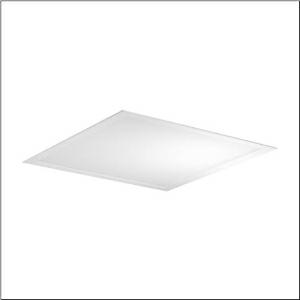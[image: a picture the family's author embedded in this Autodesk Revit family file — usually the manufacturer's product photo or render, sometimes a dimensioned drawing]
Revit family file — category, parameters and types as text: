
# Revit family: apollon_31_square_51mp11w72342
name_source: partatom
category: Lighting Fixtures
units: mm (PartAtom-declared; Revit-internal decimal feet)

## family parameters
Cut with Voids When Loaded = No
Host = Face
Light Source = No
Part Type = Normal
Room Calculation Point = No
Round Connector Dimension = Use Diameter
Shared = No

## types (1)
- Apollon 31 square (1 x LED, 3800 lm, 27.5 W, 3000K)
    Apparent Load = 28 VA
    CIE Flux Codes = 61 87 97 100 100
    Color Rendering = 80
    Color Temperature = 3000K
    Default Elevation = 1800 mm
    Description = Apollon 31 square, office luminaire, primary optical cover: micro prismatic cover, of PMMA, CAT 2 (L<= 3000cd/m²), light emission: direct distribution, primary light characteristic: symmetric, installation type: lay-in mounting, recessed, LED, rated luminous flux: 3.800lm, luminous efficacy: 138lm/W, light colour: 830, colour temperature: 3000K, control gear: ON/OFF, with terminal, 3-pole, mains connection: 220..240V, AC, 50/60Hz, rated input power: 28W, suitable for self-contained emergency lighting element 58DB00B013A with integrated self-test function according to EN 60598-2-22, housing, of aluminium, coated, traffic white (RAL 9016), module: M625, length: 620mm, width: 620mm, height: 62mm, housing upper side, of sheet steel, coated, protection rating (complete): IP20, protection rating (lamp compartment, on room side): IP40, insulation class (complete): insulation class II (safety insulation), certification: CE, ENEC, impact resistance: IK03, permissible operating ambient temperature: -20..+40°C, corresponds to IFS (International Featured Standards) requirements for safety and quality in the food industry, packaging unit: 1 piece
    Height = 0 mm  [stored 0 ft]
    Lamp = 1 x LED
    Lamp Light Flux = 3800 lm
    Lamp Power = 27.5 W
    Lamp count = 1
    Length = 620 mm
    Luminous efficacy = 138 lm/W
    Manufacturer = Siteco
    ModVariant = No
    Model = 51MP11W72342
    Mounting Place = Ceiling
    Mounting Type = Recessed
    Number of Poles = 1
    OnlyDefault = Yes
    Power Factor = 1
    Product Name = Apollon 31 square
    Product group = office luminaire | ceiling recessed
    ProductGroupID = 400
    Protection Class = Protection class II
    Protection Degree = IP 20
    RLX_Detail_Level = 1
    RLX_Emergency_Light_Flux = 0 lm
    RLX_Emergency_Type = 0
    RLX_Emergency_Type_DB = No
    RlxData = <blob elided: 13285 chars, md5=f9c1000e>
    Socket = socket
    Standby Power = 0 W
    System Light Flux = 3800 lm
    System Power = 28 W
    Type Comments = Product without accessories
    Type Image = l_1291039.jpg
    URL = http://relux.com
    VarID = ---
    Voltage = 0 V
    Weight = 0.00 kg
    Width = 620 mm

note: [stored X ft] marks values corroborated as IEEE doubles in the binary element streams (Revit-internal decimal feet)

## geometry (parser evidence)
native form markers: Sweep x11
no freeform markers — native parametric forms only
